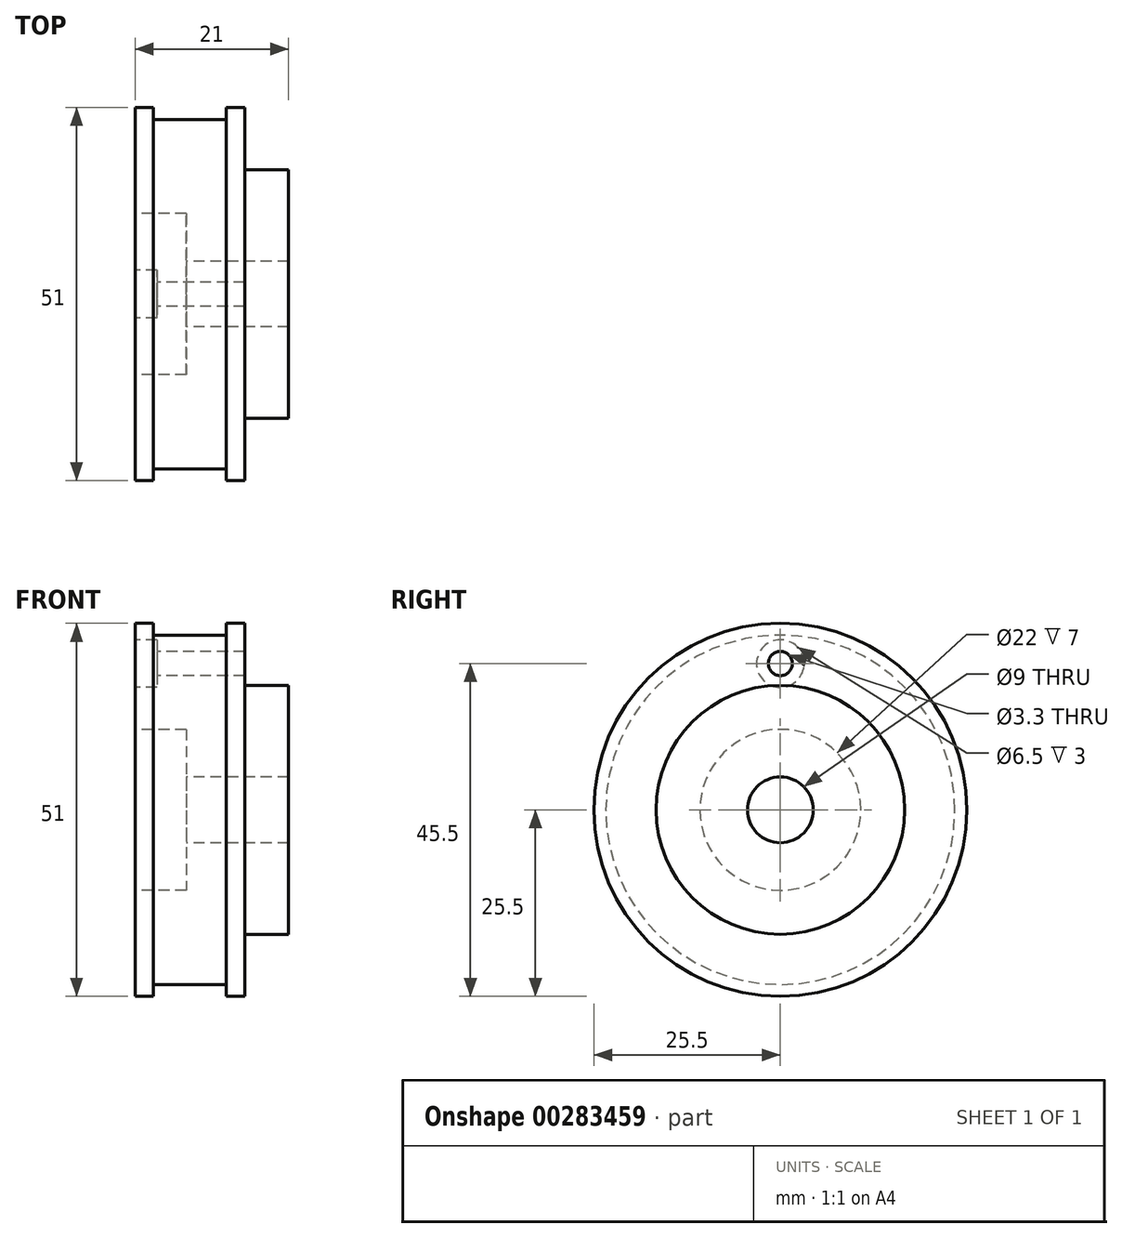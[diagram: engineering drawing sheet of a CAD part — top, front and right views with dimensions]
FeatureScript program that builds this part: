
annotation { "Feature Type Name" : "Feature", "Feature Type Description" : "" }
export const myFeature = defineFeature(function(context is Context, id is Id, definition is map)
    precondition{}
    {
        {
            var Q0;
            Q0=qCreatedBy(makeId("Front.planeOp"),FACE);
            var sketch = newSketch(context, id + "F0", { "sketchPlane" : qUnion([Q0])});
            skLineSegment(sketch, "E0", {"start": v(-32.75, 0) * mm, "end": v(34.5, 0) * mm, "construction": true});
            skLineSegment(sketch, "E1", {"start": v(6, 4.5) * mm, "end": v(-8, 4.5) * mm});
            skLineSegment(sketch, "E2", {"start": v(-15, 11) * mm, "end": v(-15, 25.5) * mm});
            skLineSegment(sketch, "E3", {"start": v(-15, 25.5) * mm, "end": v(-12.5, 25.5) * mm});
            skLineSegment(sketch, "E4", {"start": v(-12.5, 25.5) * mm, "end": v(-12.5, 23.88) * mm});
            skLineSegment(sketch, "E5", {"start": v(-12.5, 23.88) * mm, "end": v(-2.5, 23.88) * mm});
            skLineSegment(sketch, "E6", {"start": v(-2.5, 23.88) * mm, "end": v(-2.5, 25.5) * mm});
            skLineSegment(sketch, "E7", {"start": v(-2.5, 25.5) * mm, "end": v(0, 25.5) * mm});
            skLineSegment(sketch, "E8", {"start": v(0, 25.5) * mm, "end": v(0, 17) * mm});
            skLineSegment(sketch, "E9", {"start": v(0, 17) * mm, "end": v(6, 17) * mm});
            skLineSegment(sketch, "E10", {"start": v(6, 17) * mm, "end": v(6, 4.5) * mm});
            skLineSegment(sketch, "E11", {"start": v(-8, 4.5) * mm, "end": v(-8, 11) * mm});
            skLineSegment(sketch, "E12", {"start": v(-8, 11) * mm, "end": v(-15, 11) * mm});
            skSolve(sketch);
        }
        {
            var Q0;
            Q0 = qSketchRegion(id + "F0", true);
            var Q1;
            Q1=sQuery(id+"F0.wireOp",EDGE,"E0");
            revolve(context, id + "F1", {"entities" : qUnion([Q0]), "axis" : qUnion([Q1]), "revolveType" : RevolveType.FULL});
        }
        {
            var Q0;
            Q0=makeQuery(id+"F1.opRevolve","SWEPT_FACE",FACE,{"disambiguationData":[OSD([sQuery(id+"F0.wireOp",EDGE,"E2")])]});
            var sketch = newSketch(context, id + "F2", { "sketchPlane" : qUnion([Q0])});
            skPoint(sketch, "E13", {"position": v(0, 20) * mm});
            skSolve(sketch);
        }
        {
            var Q0;
            Q0=sQuery(id+"F2.wireOp",VERTEX,"E13");
            var Q1;
            Q1=makeQuery(id+"F1.opRevolve","SWEPT_BODY",BODY,{"disambiguationData":[OSD([sQuery(id+"F0.wireOp",EDGE,"E1"),sQuery(id+"F0.wireOp",EDGE,"E2"),sQuery(id+"F0.wireOp",EDGE,"E3"),sQuery(id+"F0.wireOp",EDGE,"E4"),sQuery(id+"F0.wireOp",EDGE,"E5"),sQuery(id+"F0.wireOp",EDGE,"E6"),sQuery(id+"F0.wireOp",EDGE,"E7"),sQuery(id+"F0.wireOp",EDGE,"E8"),sQuery(id+"F0.wireOp",EDGE,"E9"),sQuery(id+"F0.wireOp",EDGE,"E10"),sQuery(id+"F0.wireOp",EDGE,"E11"),sQuery(id+"F0.wireOp",EDGE,"E12")])]});
            hole(context, id + "F3", {"style" : HoleStyle.C_BORE, "endStyle" : HoleEndStyle.THROUGH, "standardTappedOrClearance" : lookupTablePath({ "standard" : "ISO", "fit" : "Normal", "size" : "M3", "type" : "Clearance" }), "standardBlindInLast" : lookupTablePath({ "fit" : "Standard", "standard" : "ISO", "size" : "M3", "type" : "Clearance" }), "holeDiameter" : 3.3 * mm, "cBoreDiameter" : 6.5 * mm, "cBoreDepth" : 3 * mm, "tappedDepth" : 12 * mm, "tapClearance" : 3, "locations" : qUnion([Q0]), "scope" : qUnion([Q1])});
        }
    });
